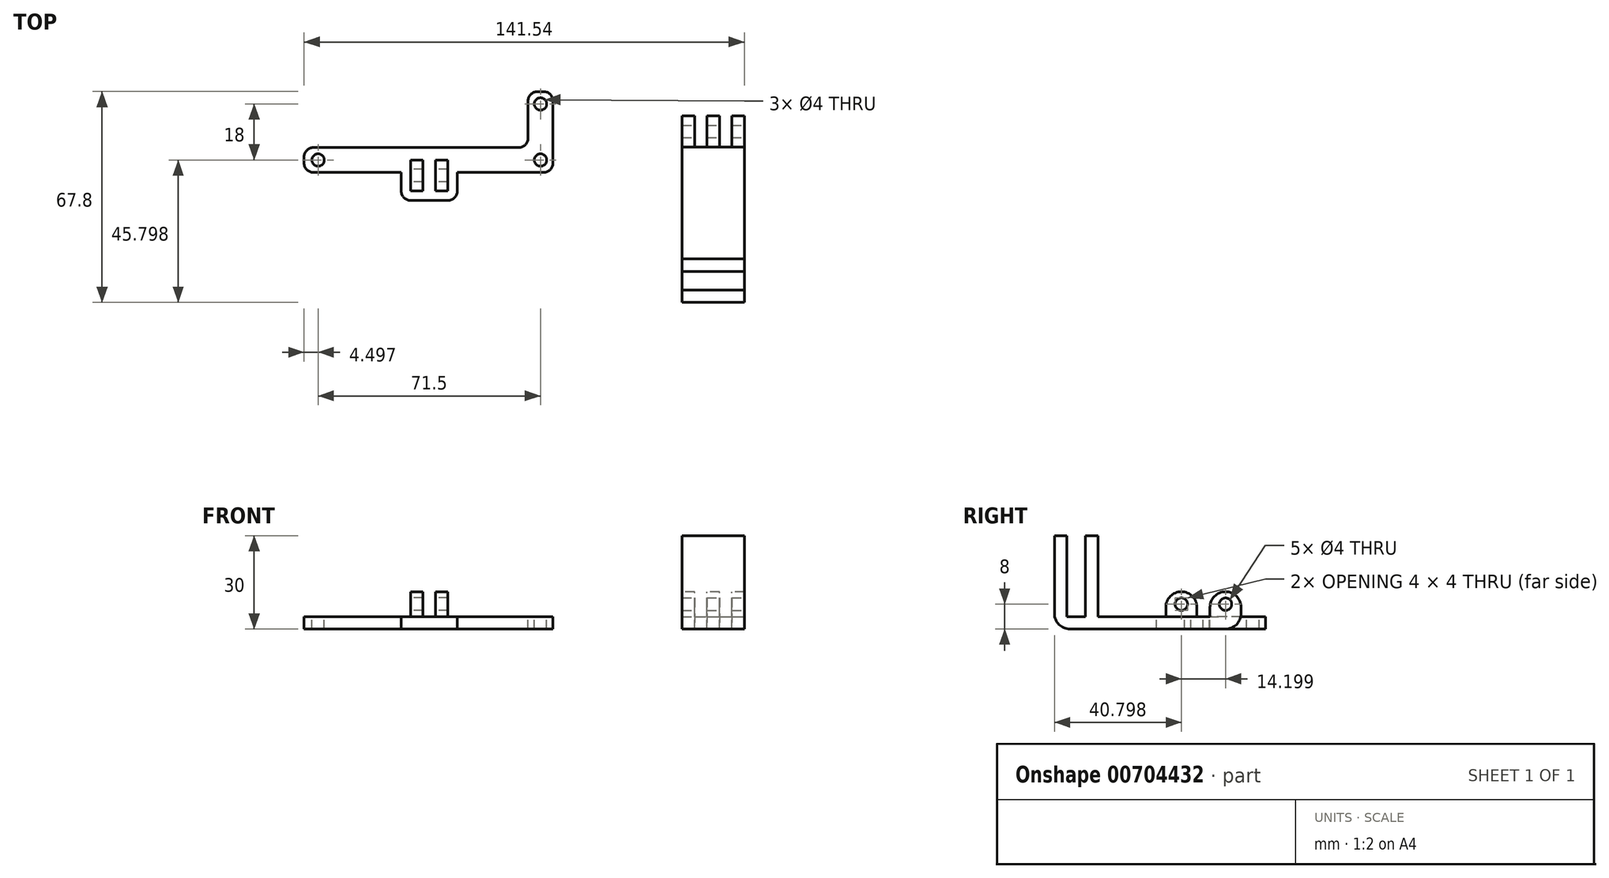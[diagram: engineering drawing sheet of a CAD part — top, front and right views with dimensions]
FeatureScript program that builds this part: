
annotation { "Feature Type Name" : "Feature", "Feature Type Description" : "" }
export const myFeature = defineFeature(function(context is Context, id is Id, definition is map)
    precondition{}
    {
        {
            var Q0;
            Q0=qCreatedBy(makeId("Top.planeOp"),FACE);
            var sketch = newSketch(context, id + "F0", { "sketchPlane" : qUnion([Q0])});
            skLineSegment(sketch, "E0.bottom", {"start": v(-89.7, 63.07) * mm, "end": v(-9.7, 63.07) * mm});
            skLineSegment(sketch, "E0.top", {"start": v(-89.7, 28.07) * mm, "end": v(-9.7, 28.07) * mm});
            skLineSegment(sketch, "E0.left", {"start": v(-89.7, 63.07) * mm, "end": v(-89.7, 28.07) * mm});
            skLineSegment(sketch, "E0.right", {"start": v(-9.7, 63.07) * mm, "end": v(-9.7, 28.07) * mm});
            skSolve(sketch);
        }
        {
            var Q0;
            Q0=makeQuery(id+"F0.imprint","IMPRINT",FACE,{"disambiguationData":[TD([[makeQuery(id+"F0.imprint","IMPRINT",EDGE,{"derivedFrom":sQuery(id+"F0.wireOp",EDGE,"E0.bottom")}),-1.0]])]});
            extrude(context, id + "F1", {"entities" : qUnion([Q0]), "depth" : 4 * mm, "offsetDistance" : 25 * mm});
        }
        {
            var Q0;
            Q0=makeQuery(id+"F1.opExtrude","CAP_FACE",FACE,{"disambiguationData":[OSD([sQuery(id+"F0.wireOp",EDGE,"E0.bottom"),sQuery(id+"F0.wireOp",EDGE,"E0.top"),sQuery(id+"F0.wireOp",EDGE,"E0.left"),sQuery(id+"F0.wireOp",EDGE,"E0.right")])],"isStart":false});
            var sketch = newSketch(context, id + "F2", { "sketchPlane" : qUnion([Q0])});
            skCircle(sketch, "E1", {"center": v(-85.2, 41.07) * mm, "radius": 2 * mm});
            skCircle(sketch, "E2", {"center": v(-13.7, 41.07) * mm, "radius": 2 * mm});
            skCircle(sketch, "E3", {"center": v(-13.7, 59.07) * mm, "radius": 2 * mm});
            skLineSegment(sketch, "E4.bottom", {"start": v(-17.7, 69.08) * mm, "end": v(-95.9, 69.08) * mm});
            skLineSegment(sketch, "E4.top", {"start": v(-17.7, 45.07) * mm, "end": v(-95.9, 45.07) * mm});
            skLineSegment(sketch, "E4.left", {"start": v(-17.7, 69.08) * mm, "end": v(-17.7, 45.07) * mm});
            skLineSegment(sketch, "E4.right", {"start": v(-95.9, 69.08) * mm, "end": v(-95.9, 45.07) * mm});
            skSolve(sketch);
        }
        {
            var Q0;
            Q0 = qSketchRegion(id + "F2", true);
            extrude(context, id + "F3", {"entities" : qUnion([Q0]), "operationType" : NewBodyOperationType.REMOVE, "oppositeDirection" : true, "depth" : 25 * mm, "offsetDistance" : 25 * mm});
        }
        {
            var Q0;
            Q0=makeQuery(id+"F1.opExtrude","CAP_FACE",FACE,{"disambiguationData":[OSD([sQuery(id+"F0.wireOp",EDGE,"E0.bottom"),sQuery(id+"F0.wireOp",EDGE,"E0.top"),sQuery(id+"F0.wireOp",EDGE,"E0.left"),sQuery(id+"F0.wireOp",EDGE,"E0.right")])],"isStart":false});
            var sketch = newSketch(context, id + "F4", { "sketchPlane" : qUnion([Q0])});
            skLineSegment(sketch, "E5", {"start": v(-85.2, 41.07) * mm, "end": v(-13.7, 41.07) * mm, "construction": true});
            skLineSegment(sketch, "E6", {"start": v(-49.44, 41.07) * mm, "end": v(-49.44, 36.07) * mm, "construction": true});
            skLineSegment(sketch, "E7.bottom", {"start": v(-43.44, 41.07) * mm, "end": v(-55.44, 41.07) * mm});
            skLineSegment(sketch, "E7.top", {"start": v(-43.44, 31.07) * mm, "end": v(-55.44, 31.07) * mm});
            skLineSegment(sketch, "E7.left", {"start": v(-43.44, 41.07) * mm, "end": v(-43.44, 31.07) * mm});
            skLineSegment(sketch, "E7.right", {"start": v(-55.44, 41.07) * mm, "end": v(-55.44, 31.07) * mm});
            skPoint(sketch, "E7.middle", {"position": v(-49.44, 36.07) * mm});
            skLineSegment(sketch, "E8.bottom", {"start": v(-47.44, 41.07) * mm, "end": v(-51.44, 41.07) * mm});
            skLineSegment(sketch, "E8.top", {"start": v(-47.44, 31.07) * mm, "end": v(-51.44, 31.07) * mm});
            skLineSegment(sketch, "E8.left", {"start": v(-47.44, 41.07) * mm, "end": v(-47.44, 31.07) * mm});
            skLineSegment(sketch, "E8.right", {"start": v(-51.44, 41.07) * mm, "end": v(-51.44, 31.07) * mm});
            skSolve(sketch);
        }
        {
            var Q0;
            {var subQ0=sQuery(id+"F4.wireOp",EDGE,"E7.right");Q0=makeQuery(id+"F4.imprint","IMPRINT",FACE,{"disambiguationData":[TD([[makeQuery(id+"F4.imprint","IMPRINT",EDGE,{"derivedFrom":subQ0}),1.0]])]});}
            var Q1;
            {var subQ0=sQuery(id+"F4.wireOp",EDGE,"E7.left");Q1=makeQuery(id+"F4.imprint","IMPRINT",FACE,{"disambiguationData":[TD([[makeQuery(id+"F4.imprint","IMPRINT",EDGE,{"derivedFrom":subQ0}),-1.0]])]});}
            extrude(context, id + "F5", {"entities" : qUnion([Q0, Q1]), "operationType" : NewBodyOperationType.ADD, "depth" : 8 * mm, "offsetDistance" : 25 * mm});
        }
        {
            var Q0;
            Q0=makeQuery(id+"F5.opExtrude","SWEPT_FACE",FACE,{"disambiguationData":[OSD([sQuery(id+"F4.wireOp",EDGE,"E7.right")])]});
            var sketch = newSketch(context, id + "F6", { "sketchPlane" : qUnion([Q0])});
            skCircle(sketch, "E9", {"center": v(-36.07, 8) * mm, "radius": 2 * mm});
            skPoint(sketch, "E9.centerSnap0", {"position": v(-41.07, 8) * mm});
            skPoint(sketch, "E9.centerSnap1", {"position": v(-36.07, 12) * mm});
            skSolve(sketch);
        }
        {
            var Q0;
            Q0=makeQuery(id+"F6.imprint","IMPRINT",FACE,{"disambiguationData":[TD([[makeQuery(id+"F6.imprint","IMPRINT",EDGE,{"derivedFrom":sQuery(id+"F6.wireOp",EDGE,"E9")}),1.0]])]});
            extrude(context, id + "F7", {"entities" : qUnion([Q0]), "operationType" : NewBodyOperationType.REMOVE, "oppositeDirection" : true, "depth" : 12 * mm, "offsetDistance" : 25 * mm});
        }
        {
            var Q0;
            {var subQ0=sQuery(id+"F4.wireOp",EDGE,"E7.bottom");Q0=makeQuery(id+"F5.opExtrude","CAP_EDGE",EDGE,{"disambiguationData":[OSD([subQ0]),TDD([makeQuery(id+"F4.imprint","IMPRINT",EDGE,{"disambiguationData":[TD([[makeQuery(id+"F4.imprint","INTERSECT",VERTEX,{"derivedFrom":[subQ0,sQuery(id+"F4.wireOp",EDGE,"E7.right")]}),1.0]])],"derivedFrom":subQ0})])],"isStart":false});}
            var Q1;
            {var subQ0=sQuery(id+"F4.wireOp",EDGE,"E7.bottom");Q1=makeQuery(id+"F5.opExtrude","CAP_EDGE",EDGE,{"disambiguationData":[OSD([subQ0]),TDD([makeQuery(id+"F4.imprint","IMPRINT",EDGE,{"disambiguationData":[TD([[makeQuery(id+"F4.imprint","INTERSECT",VERTEX,{"derivedFrom":[subQ0,sQuery(id+"F4.wireOp",EDGE,"E7.left")]}),-1.0]])],"derivedFrom":subQ0})])],"isStart":false});}
            var Q2;
            {var subQ0=sQuery(id+"F4.wireOp",EDGE,"E7.top");Q2=makeQuery(id+"F5.opExtrude","CAP_EDGE",EDGE,{"disambiguationData":[OSD([subQ0]),TDD([makeQuery(id+"F4.imprint","IMPRINT",EDGE,{"disambiguationData":[TD([[makeQuery(id+"F4.imprint","INTERSECT",VERTEX,{"derivedFrom":[subQ0,sQuery(id+"F4.wireOp",EDGE,"E7.right")]}),1.0]])],"derivedFrom":subQ0})])],"isStart":false});}
            var Q3;
            {var subQ0=sQuery(id+"F4.wireOp",EDGE,"E7.top");Q3=makeQuery(id+"F5.opExtrude","CAP_EDGE",EDGE,{"disambiguationData":[OSD([subQ0]),TDD([makeQuery(id+"F4.imprint","IMPRINT",EDGE,{"disambiguationData":[TD([[makeQuery(id+"F4.imprint","INTERSECT",VERTEX,{"derivedFrom":[subQ0,sQuery(id+"F4.wireOp",EDGE,"E7.left")]}),-1.0]])],"derivedFrom":subQ0})])],"isStart":false});}
            fillet(context, id + "F8", {"entities" : qUnion([Q0, Q1, Q2, Q3]), "radius" : 5 * mm, "tangentPropagation" : true, "allowEdgeOverflow" : false});
        }
        {
            var Q0;
            Q0=makeQuery(id+"F1.opExtrude","CAP_FACE",FACE,{"disambiguationData":[OSD([sQuery(id+"F0.wireOp",EDGE,"E0.bottom"),sQuery(id+"F0.wireOp",EDGE,"E0.top"),sQuery(id+"F0.wireOp",EDGE,"E0.left"),sQuery(id+"F0.wireOp",EDGE,"E0.right")])],"isStart":false});
            var sketch = newSketch(context, id + "F9", { "sketchPlane" : qUnion([Q0])});
            skLineSegment(sketch, "E10.bottom", {"start": v(-102.88, 37.07) * mm, "end": v(-58.44, 37.07) * mm});
            skLineSegment(sketch, "E10.top", {"start": v(-102.88, 18.95) * mm, "end": v(-58.44, 18.95) * mm});
            skLineSegment(sketch, "E10.left", {"start": v(-102.88, 37.07) * mm, "end": v(-102.88, 18.95) * mm});
            skLineSegment(sketch, "E10.right", {"start": v(-58.44, 37.07) * mm, "end": v(-58.44, 18.95) * mm});
            skLineSegment(sketch, "E11.bottom", {"start": v(-40.44, 37.07) * mm, "end": v(3.45, 37.07) * mm});
            skLineSegment(sketch, "E11.top", {"start": v(-40.44, 16.96) * mm, "end": v(3.45, 16.96) * mm});
            skLineSegment(sketch, "E11.left", {"start": v(-40.44, 37.07) * mm, "end": v(-40.44, 16.96) * mm});
            skLineSegment(sketch, "E11.right", {"start": v(3.45, 37.07) * mm, "end": v(3.45, 16.96) * mm});
            skLineSegment(sketch, "E12", {"start": v(-55.44, 33.1) * mm, "end": v(-58.44, 33.1) * mm, "construction": true});
            skLineSegment(sketch, "E13", {"start": v(-43.44, 32.9) * mm, "end": v(-40.44, 32.9) * mm, "construction": true});
            skLineSegment(sketch, "E14", {"start": v(-45.44, 31.07) * mm, "end": v(-45.44, 28.07) * mm, "construction": true});
            skSolve(sketch);
        }
        {
            var Q0;
            {var subQ1=sQuery(id+"F9.wireOp",EDGE,"E10.top");Q0=makeQuery(id+"F9.imprint","IMPRINT",FACE,{"disambiguationData":[TD([[makeQuery(id+"F9.imprint","IMPRINT",EDGE,{"derivedFrom":subQ1}),1.0]])]});}
            var Q1;
            {var subQ2=sQuery(id+"F9.wireOp",EDGE,"E11.top");Q1=makeQuery(id+"F9.imprint","IMPRINT",FACE,{"disambiguationData":[TD([[makeQuery(id+"F9.imprint","IMPRINT",EDGE,{"derivedFrom":subQ2}),1.0]])]});}
            var Q2;
            {var subQ0=sQuery(id+"F9.wireOp",EDGE,"E11.left");var subQ1=sQuery(id+"F9.wireOp",EDGE,"E11.bottom");var subQ2=makeQuery(id+"F9.imprint","INTERSECT",VERTEX,{"derivedFrom":[subQ1,subQ0]});Q2=makeQuery(id+"F9.imprint","IMPRINT",FACE,{"disambiguationData":[TD([[makeQuery(id+"F9.imprint","IMPRINT",EDGE,{"disambiguationData":[TD([[subQ2,-1.0]])],"derivedFrom":subQ1}),-1.0]])]});}
            var Q3;
            {var subQ0=sQuery(id+"F9.wireOp",EDGE,"E10.right");var subQ1=sQuery(id+"F9.wireOp",EDGE,"E10.bottom");var subQ2=makeQuery(id+"F9.imprint","INTERSECT",VERTEX,{"derivedFrom":[subQ1,subQ0]});Q3=makeQuery(id+"F9.imprint","IMPRINT",FACE,{"disambiguationData":[TD([[makeQuery(id+"F9.imprint","IMPRINT",EDGE,{"disambiguationData":[TD([[subQ2,1.0]])],"derivedFrom":subQ1}),-1.0]])]});}
            extrude(context, id + "F10", {"entities" : qUnion([Q0, Q1, Q2, Q3]), "operationType" : NewBodyOperationType.REMOVE, "oppositeDirection" : true, "depth" : 25 * mm, "offsetDistance" : 25 * mm});
        }
        {
            var Q0;
            Q0=makeQuery(id+"F3.boolean.opBoolean","INTERSECT",EDGE,{"derivedFrom":[makeQuery(id+"F1.opExtrude","SWEPT_FACE",FACE,{"disambiguationData":[OSD([sQuery(id+"F0.wireOp",EDGE,"E0.left")])]}),makeQuery(id+"F3.opExtrude","SWEPT_FACE",FACE,{"disambiguationData":[OSD([sQuery(id+"F2.wireOp",EDGE,"E4.top")])]})]});
            var Q1;
            Q1=makeQuery(id+"F10.boolean.opBoolean","INTERSECT",EDGE,{"derivedFrom":[makeQuery(id+"F1.opExtrude","SWEPT_FACE",FACE,{"disambiguationData":[OSD([sQuery(id+"F0.wireOp",EDGE,"E0.left")])]}),makeQuery(id+"F10.opExtrude","SWEPT_FACE",FACE,{"disambiguationData":[OSD([sQuery(id+"F9.wireOp",EDGE,"E10.bottom")])]})]});
            var Q2;
            Q2=makeQuery(id+"F10.boolean.opBoolean","INTERSECT",EDGE,{"derivedFrom":[makeQuery(id+"F1.opExtrude","SWEPT_FACE",FACE,{"disambiguationData":[OSD([sQuery(id+"F0.wireOp",EDGE,"E0.top")])]}),makeQuery(id+"F10.opExtrude","SWEPT_FACE",FACE,{"disambiguationData":[OSD([sQuery(id+"F9.wireOp",EDGE,"E10.right")])]})]});
            var Q3;
            Q3=makeQuery(id+"F10.boolean.opBoolean","INTERSECT",EDGE,{"derivedFrom":[makeQuery(id+"F1.opExtrude","SWEPT_FACE",FACE,{"disambiguationData":[OSD([sQuery(id+"F0.wireOp",EDGE,"E0.top")])]}),makeQuery(id+"F10.opExtrude","SWEPT_FACE",FACE,{"disambiguationData":[OSD([sQuery(id+"F9.wireOp",EDGE,"E11.left")])]})]});
            var Q4;
            Q4=makeQuery(id+"F10.boolean.opBoolean","INTERSECT",EDGE,{"derivedFrom":[makeQuery(id+"F1.opExtrude","SWEPT_FACE",FACE,{"disambiguationData":[OSD([sQuery(id+"F0.wireOp",EDGE,"E0.right")])]}),makeQuery(id+"F10.opExtrude","SWEPT_FACE",FACE,{"disambiguationData":[OSD([sQuery(id+"F9.wireOp",EDGE,"E11.bottom")])]})]});
            var Q5;
            Q5=makeQuery(id+"F1.opExtrude","SWEPT_EDGE",EDGE,{"disambiguationData":[OSD([sQuery(id+"F0.wireOp",EDGE,"E0.bottom"),sQuery(id+"F0.wireOp",EDGE,"E0.right")])]});
            var Q6;
            Q6=makeQuery(id+"F3.boolean.opBoolean","INTERSECT",EDGE,{"derivedFrom":[makeQuery(id+"F1.opExtrude","SWEPT_FACE",FACE,{"disambiguationData":[OSD([sQuery(id+"F0.wireOp",EDGE,"E0.bottom")])]}),makeQuery(id+"F3.opExtrude","SWEPT_FACE",FACE,{"disambiguationData":[OSD([sQuery(id+"F2.wireOp",EDGE,"E4.left")])]})]});
            var Q7;
            Q7=makeQuery(id+"F3.boolean.opBoolean","COPY",EDGE,{"derivedFrom":makeQuery(id+"F3.opExtrude","SWEPT_EDGE",EDGE,{"disambiguationData":[OSD([sQuery(id+"F2.wireOp",EDGE,"E4.top"),sQuery(id+"F2.wireOp",EDGE,"E4.left")])]})});
            fillet(context, id + "F11", {"entities" : qUnion([Q0, Q1, Q2, Q3, Q4, Q5, Q6, Q7]), "radius" : 3 * mm, "tangentPropagation" : true, "allowEdgeOverflow" : false});
        }
        {
            var Q0;
            Q0=qCreatedBy(makeId("Top.planeOp"),FACE);
            var sketch = newSketch(context, id + "F12", { "sketchPlane" : qUnion([Q0])});
            skLineSegment(sketch, "E15.bottom", {"start": v(31.85, 55.27) * mm, "end": v(51.85, 55.27) * mm});
            skLineSegment(sketch, "E15.top", {"start": v(31.85, -4.73) * mm, "end": v(51.85, -4.73) * mm});
            skLineSegment(sketch, "E15.left", {"start": v(31.85, 55.27) * mm, "end": v(31.85, -4.73) * mm});
            skLineSegment(sketch, "E15.right", {"start": v(51.85, 55.27) * mm, "end": v(51.85, -4.73) * mm});
            skSolve(sketch);
        }
        {
            var Q0;
            Q0=makeQuery(id+"F12.imprint","IMPRINT",FACE,{"disambiguationData":[TD([[makeQuery(id+"F12.imprint","IMPRINT",EDGE,{"derivedFrom":sQuery(id+"F12.wireOp",EDGE,"E15.bottom")}),-1.0]])]});
            extrude(context, id + "F13", {"entities" : qUnion([Q0]), "depth" : 4 * mm, "offsetDistance" : 25 * mm});
        }
        {
            var Q0;
            Q0=makeQuery(id+"F13.opExtrude","SWEPT_FACE",FACE,{"disambiguationData":[OSD([sQuery(id+"F12.wireOp",EDGE,"E15.right")])]});
            var sketch = newSketch(context, id + "F14", { "sketchPlane" : qUnion([Q0])});
            skLineSegment(sketch, "E16.bottom", {"start": v(55.27, 4) * mm, "end": v(45.27, 4) * mm});
            skLineSegment(sketch, "E16.top", {"start": v(55.27, 12) * mm, "end": v(45.27, 12) * mm});
            skLineSegment(sketch, "E16.left", {"start": v(55.27, 4) * mm, "end": v(55.27, 12) * mm});
            skLineSegment(sketch, "E16.right", {"start": v(45.27, 4) * mm, "end": v(45.27, 12) * mm});
            skLineSegment(sketch, "E17.bottom", {"start": v(-4.73, 4) * mm, "end": v(9.27, 4) * mm});
            skLineSegment(sketch, "E17.top", {"start": v(-4.73, 30) * mm, "end": v(9.27, 30) * mm});
            skLineSegment(sketch, "E17.left", {"start": v(-4.73, 4) * mm, "end": v(-4.73, 30) * mm});
            skLineSegment(sketch, "E17.right", {"start": v(9.27, 4) * mm, "end": v(9.27, 30) * mm});
            skSolve(sketch);
        }
        {
            var Q0;
            Q0=makeQuery(id+"F14.imprint","IMPRINT",FACE,{"disambiguationData":[TD([[makeQuery(id+"F14.imprint","IMPRINT",EDGE,{"derivedFrom":sQuery(id+"F14.wireOp",EDGE,"E16.bottom")}),-1.0]])]});
            var Q1;
            Q1=makeQuery(id+"F14.imprint","IMPRINT",FACE,{"disambiguationData":[TD([[makeQuery(id+"F14.imprint","IMPRINT",EDGE,{"derivedFrom":sQuery(id+"F14.wireOp",EDGE,"E17.bottom")}),-1.0]])]});
            extrude(context, id + "F15", {"entities" : qUnion([Q0, Q1]), "operationType" : NewBodyOperationType.ADD, "oppositeDirection" : true, "depth" : 20 * mm, "offsetDistance" : 25 * mm});
        }
        {
            var Q0;
            Q0=makeQuery(id+"F15.boolean.opBoolean","MERGE",FACE,{"derivedFrom":[makeQuery(id+"F13.opExtrude","SWEPT_FACE",FACE,{"disambiguationData":[OSD([sQuery(id+"F12.wireOp",EDGE,"E15.right")])]}),makeQuery(id+"F15.opExtrude","CAP_FACE",FACE,{"disambiguationData":[OSD([sQuery(id+"F14.wireOp",EDGE,"E16.bottom"),sQuery(id+"F14.wireOp",EDGE,"E16.top"),sQuery(id+"F14.wireOp",EDGE,"E16.left"),sQuery(id+"F14.wireOp",EDGE,"E16.right")])],"isStart":true})]});
            var sketch = newSketch(context, id + "F16", { "sketchPlane" : qUnion([Q0])});
            skCircle(sketch, "E18", {"center": v(50.27, 8) * mm, "radius": 2 * mm});
            skPoint(sketch, "E18.centerSnap0", {"position": v(50.27, 12) * mm});
            skPoint(sketch, "E18.centerSnap1", {"position": v(45.27, 8) * mm});
            skLineSegment(sketch, "E19.bottom", {"start": v(-0.73, 30) * mm, "end": v(5.27, 30) * mm});
            skLineSegment(sketch, "E19.top", {"start": v(-0.73, 4) * mm, "end": v(5.27, 4) * mm});
            skLineSegment(sketch, "E19.left", {"start": v(-0.73, 30) * mm, "end": v(-0.73, 4) * mm});
            skLineSegment(sketch, "E19.right", {"start": v(5.27, 30) * mm, "end": v(5.27, 4) * mm});
            skSolve(sketch);
        }
        {
            var Q0;
            Q0=makeQuery(id+"F16.imprint","IMPRINT",FACE,{"disambiguationData":[TD([[makeQuery(id+"F16.imprint","IMPRINT",EDGE,{"derivedFrom":sQuery(id+"F16.wireOp",EDGE,"E18")}),1.0]])]});
            var Q1;
            Q1=makeQuery(id+"F16.imprint","IMPRINT",FACE,{"disambiguationData":[TD([[makeQuery(id+"F16.imprint","IMPRINT",EDGE,{"derivedFrom":sQuery(id+"F16.wireOp",EDGE,"E19.bottom")}),-1.0]])]});
            extrude(context, id + "F17", {"entities" : qUnion([Q0, Q1]), "operationType" : NewBodyOperationType.REMOVE, "oppositeDirection" : true, "depth" : 20 * mm, "offsetDistance" : 25 * mm});
        }
        {
            var Q0;
            Q0=makeQuery(id+"F15.opExtrude","SWEPT_FACE",FACE,{"disambiguationData":[OSD([sQuery(id+"F14.wireOp",EDGE,"E16.top")])]});
            var sketch = newSketch(context, id + "F18", { "sketchPlane" : qUnion([Q0])});
            skLineSegment(sketch, "E20.bottom", {"start": v(35.85, 55.27) * mm, "end": v(39.85, 55.27) * mm});
            skLineSegment(sketch, "E20.top", {"start": v(35.85, 45.27) * mm, "end": v(39.85, 45.27) * mm});
            skLineSegment(sketch, "E20.left", {"start": v(35.85, 55.27) * mm, "end": v(35.85, 45.27) * mm});
            skLineSegment(sketch, "E20.right", {"start": v(39.85, 55.27) * mm, "end": v(39.85, 45.27) * mm});
            skLineSegment(sketch, "E21.bottom", {"start": v(43.85, 55.27) * mm, "end": v(47.85, 55.27) * mm});
            skLineSegment(sketch, "E21.top", {"start": v(43.85, 45.27) * mm, "end": v(47.85, 45.27) * mm});
            skLineSegment(sketch, "E21.left", {"start": v(43.85, 55.27) * mm, "end": v(43.85, 45.27) * mm});
            skLineSegment(sketch, "E21.right", {"start": v(47.85, 55.27) * mm, "end": v(47.85, 45.27) * mm});
            skSolve(sketch);
        }
        {
            var Q0;
            Q0=makeQuery(id+"F18.imprint","IMPRINT",FACE,{"disambiguationData":[TD([[makeQuery(id+"F18.imprint","IMPRINT",EDGE,{"derivedFrom":sQuery(id+"F18.wireOp",EDGE,"E20.bottom")}),-1.0]])]});
            var Q1;
            Q1=makeQuery(id+"F18.imprint","IMPRINT",FACE,{"disambiguationData":[TD([[makeQuery(id+"F18.imprint","IMPRINT",EDGE,{"derivedFrom":sQuery(id+"F18.wireOp",EDGE,"E21.bottom")}),-1.0]])]});
            extrude(context, id + "F19", {"entities" : qUnion([Q0, Q1]), "operationType" : NewBodyOperationType.REMOVE, "oppositeDirection" : true, "depth" : 12 * mm, "offsetDistance" : 25 * mm});
        }
        {
            var Q0;
            Q0=makeQuery(id+"F13.opExtrude","CAP_EDGE",EDGE,{"disambiguationData":[OSD([sQuery(id+"F12.wireOp",EDGE,"E15.top")])],"isStart":true});
            var Q1;
            {var subQ0=sQuery(id+"F14.wireOp",EDGE,"E16.right");var subQ1=sQuery(id+"F14.wireOp",EDGE,"E16.top");Q1=makeQuery(id+"F19.boolean.opBoolean","SPLIT",EDGE,{"disambiguationData":[TD([makeQuery(id+"F13.opExtrude","SWEPT_FACE",FACE,{"disambiguationData":[OSD([sQuery(id+"F12.wireOp",EDGE,"E15.right")])]})])],"derivedFrom":makeQuery(id+"F15.opExtrude","SWEPT_EDGE",EDGE,{"disambiguationData":[OSD([subQ1,subQ0])]})});}
            var Q2;
            {var subQ0=sQuery(id+"F14.wireOp",EDGE,"E16.top");var subQ1=sQuery(id+"F14.wireOp",EDGE,"E16.left");Q2=makeQuery(id+"F19.boolean.opBoolean","SPLIT",EDGE,{"disambiguationData":[TD([makeQuery(id+"F13.opExtrude","SWEPT_FACE",FACE,{"disambiguationData":[OSD([sQuery(id+"F12.wireOp",EDGE,"E15.right")])]})])],"derivedFrom":makeQuery(id+"F15.opExtrude","SWEPT_EDGE",EDGE,{"disambiguationData":[OSD([subQ0,subQ1])]})});}
            var Q3;
            {var subQ0=sQuery(id+"F14.wireOp",EDGE,"E16.top");var subQ1=sQuery(id+"F14.wireOp",EDGE,"E16.right");Q3=makeQuery(id+"F19.boolean.opBoolean","SPLIT",EDGE,{"disambiguationData":[TD([makeQuery(id+"F19.opExtrude","SWEPT_FACE",FACE,{"disambiguationData":[OSD([sQuery(id+"F18.wireOp",EDGE,"E20.right")])]})])],"derivedFrom":makeQuery(id+"F15.opExtrude","SWEPT_EDGE",EDGE,{"disambiguationData":[OSD([subQ0,subQ1])]})});}
            var Q4;
            {var subQ0=sQuery(id+"F14.wireOp",EDGE,"E16.left");var subQ1=sQuery(id+"F14.wireOp",EDGE,"E16.top");Q4=makeQuery(id+"F19.boolean.opBoolean","SPLIT",EDGE,{"disambiguationData":[TD([makeQuery(id+"F19.opExtrude","SWEPT_FACE",FACE,{"disambiguationData":[OSD([sQuery(id+"F18.wireOp",EDGE,"E20.right")])]})])],"derivedFrom":makeQuery(id+"F15.opExtrude","SWEPT_EDGE",EDGE,{"disambiguationData":[OSD([subQ1,subQ0])]})});}
            var Q5;
            {var subQ0=sQuery(id+"F14.wireOp",EDGE,"E16.right");var subQ1=sQuery(id+"F14.wireOp",EDGE,"E16.top");Q5=makeQuery(id+"F19.boolean.opBoolean","SPLIT",EDGE,{"disambiguationData":[TD([makeQuery(id+"F13.opExtrude","SWEPT_FACE",FACE,{"disambiguationData":[OSD([sQuery(id+"F12.wireOp",EDGE,"E15.left")])]})])],"derivedFrom":makeQuery(id+"F15.opExtrude","SWEPT_EDGE",EDGE,{"disambiguationData":[OSD([subQ1,subQ0])]})});}
            var Q6;
            {var subQ0=sQuery(id+"F14.wireOp",EDGE,"E16.top");var subQ1=sQuery(id+"F14.wireOp",EDGE,"E16.left");Q6=makeQuery(id+"F19.boolean.opBoolean","SPLIT",EDGE,{"disambiguationData":[TD([makeQuery(id+"F13.opExtrude","SWEPT_FACE",FACE,{"disambiguationData":[OSD([sQuery(id+"F12.wireOp",EDGE,"E15.left")])]})])],"derivedFrom":makeQuery(id+"F15.opExtrude","SWEPT_EDGE",EDGE,{"disambiguationData":[OSD([subQ0,subQ1])]})});}
            var Q7;
            {var subQ1=sQuery(id+"F12.wireOp",EDGE,"E15.right");var subQ2=sQuery(id+"F12.wireOp",EDGE,"E15.bottom");Q7=makeQuery(id+"F19.boolean.opBoolean","SPLIT",EDGE,{"disambiguationData":[TD([makeQuery(id+"F13.opExtrude","SWEPT_FACE",FACE,{"disambiguationData":[OSD([subQ1])]})])],"derivedFrom":makeQuery(id+"F13.opExtrude","CAP_EDGE",EDGE,{"disambiguationData":[OSD([subQ2])],"isStart":true})});}
            var Q8;
            {var subQ0=sQuery(id+"F12.wireOp",EDGE,"E15.bottom");Q8=makeQuery(id+"F19.boolean.opBoolean","SPLIT",EDGE,{"disambiguationData":[TD([makeQuery(id+"F19.opExtrude","SWEPT_FACE",FACE,{"disambiguationData":[OSD([sQuery(id+"F18.wireOp",EDGE,"E20.right")])]})])],"derivedFrom":makeQuery(id+"F13.opExtrude","CAP_EDGE",EDGE,{"disambiguationData":[OSD([subQ0])],"isStart":true})});}
            var Q9;
            {var subQ0=sQuery(id+"F12.wireOp",EDGE,"E15.left");var subQ1=sQuery(id+"F12.wireOp",EDGE,"E15.bottom");Q9=makeQuery(id+"F19.boolean.opBoolean","SPLIT",EDGE,{"disambiguationData":[TD([makeQuery(id+"F13.opExtrude","SWEPT_FACE",FACE,{"disambiguationData":[OSD([subQ0])]})])],"derivedFrom":makeQuery(id+"F13.opExtrude","CAP_EDGE",EDGE,{"disambiguationData":[OSD([subQ1])],"isStart":true})});}
            fillet(context, id + "F20", {"entities" : qUnion([Q0, Q1, Q2, Q3, Q4, Q5, Q6, Q7, Q8, Q9]), "radius" : 5 * mm, "tangentPropagation" : true, "allowEdgeOverflow" : false});
        }
    });
